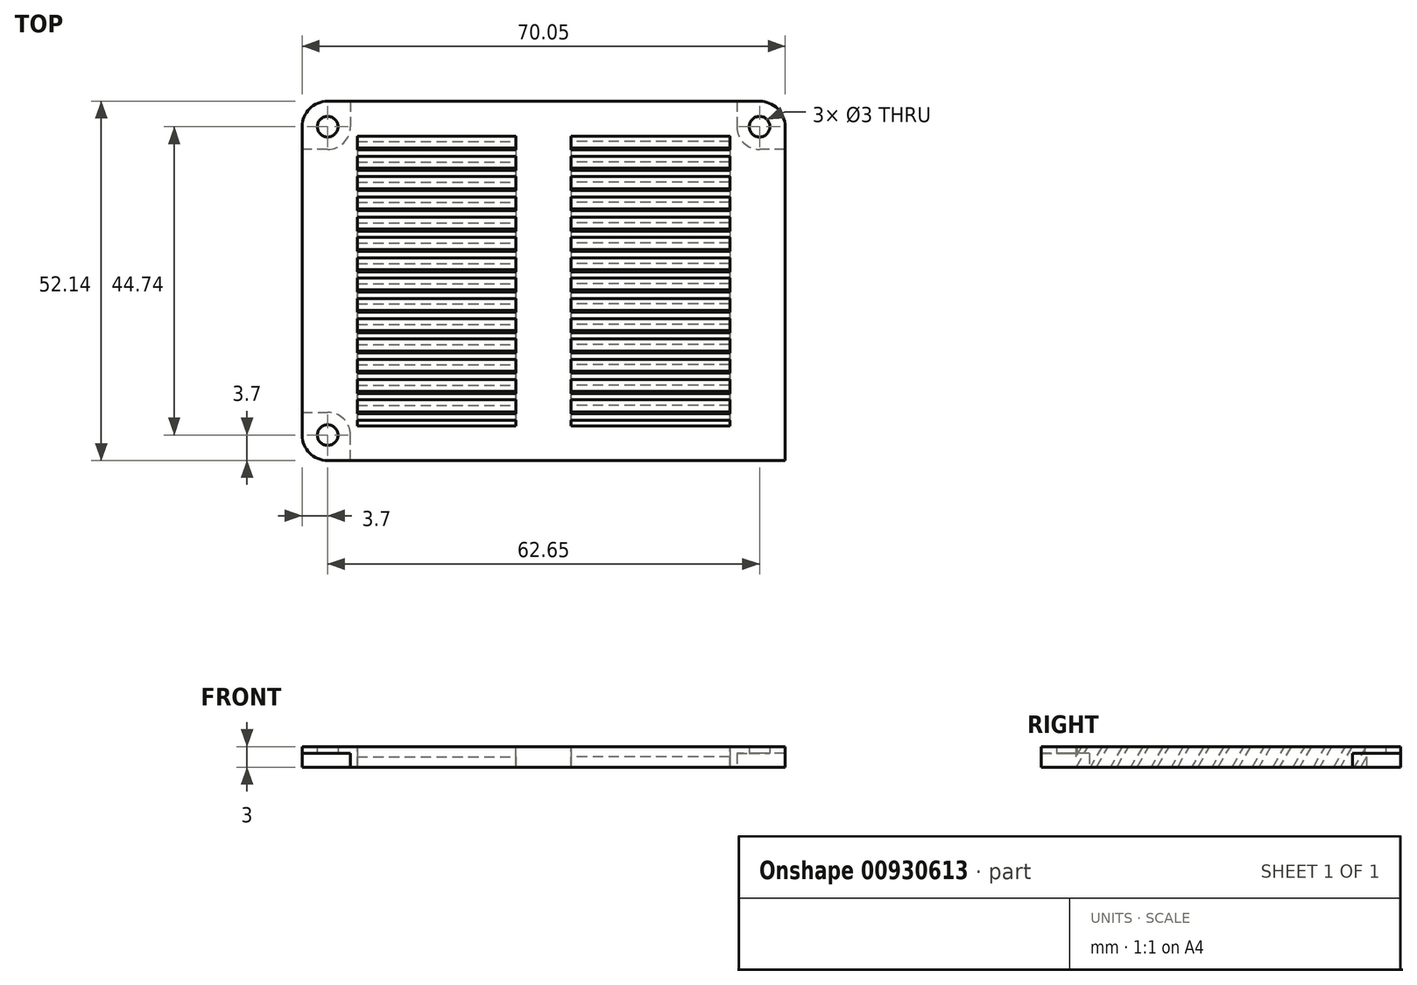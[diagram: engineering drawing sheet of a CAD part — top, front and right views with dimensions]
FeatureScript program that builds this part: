
annotation { "Feature Type Name" : "Feature", "Feature Type Description" : "" }
export const myFeature = defineFeature(function(context is Context, id is Id, definition is map)
    precondition{}
    {
        {
            var Q0;
            Q0=qCreatedBy(makeId("Top.planeOp"),FACE);
            var sketch = newSketch(context, id + "F0", { "sketchPlane" : qUnion([Q0])});
            skLineSegment(sketch, "E0", {"start": v(0, 0) * mm, "end": v(0, 44.74) * mm, "construction": true});
            skArc(sketch, "E1", {"start": v(4, 48.74) * mm, "mid": v(1.17, 47.57) * mm, "end": v(0, 44.74) * mm, "construction": true});
            skLineSegment(sketch, "E2", {"start": v(4, 48.74) * mm, "end": v(66.65, 48.74) * mm, "construction": true});
            skArc(sketch, "E3", {"start": v(70.65, 44.74) * mm, "mid": v(69.48, 47.57) * mm, "end": v(66.65, 48.74) * mm, "construction": true});
            skLineSegment(sketch, "E4", {"start": v(70.65, 44.74) * mm, "end": v(70.65, -4) * mm, "construction": true});
            skLineSegment(sketch, "E5", {"start": v(70.65, -4) * mm, "end": v(4, -4) * mm, "construction": true});
            skArc(sketch, "E6", {"start": v(0, 0) * mm, "mid": v(1.17, -2.83) * mm, "end": v(4, -4) * mm, "construction": true});
            skCircle(sketch, "E7", {"center": v(4, 44.74) * mm, "radius": 1.2 * mm, "construction": true});
            skCircle(sketch, "E8", {"center": v(4, 0) * mm, "radius": 1.2 * mm, "construction": true});
            skCircle(sketch, "E9", {"center": v(66.65, 44.74) * mm, "radius": 1.2 * mm, "construction": true});
            skLineSegment(sketch, "E10", {"start": v(0, 41.74) * mm, "end": v(4, 41.74) * mm, "construction": true});
            skLineSegment(sketch, "E11", {"start": v(7, 48.74) * mm, "end": v(7, 44.74) * mm, "construction": true});
            skArc(sketch, "E12", {"start": v(4, 41.74) * mm, "mid": v(6.12, 42.62) * mm, "end": v(7, 44.74) * mm, "construction": true});
            skLineSegment(sketch, "E13", {"start": v(63.65, 48.74) * mm, "end": v(63.65, 44.74) * mm, "construction": true});
            skLineSegment(sketch, "E14", {"start": v(70.65, 41.74) * mm, "end": v(66.65, 41.74) * mm, "construction": true});
            skArc(sketch, "E15", {"start": v(63.65, 44.74) * mm, "mid": v(64.53, 42.62) * mm, "end": v(66.65, 41.74) * mm, "construction": true});
            skLineSegment(sketch, "E16", {"start": v(0, 3) * mm, "end": v(4, 3) * mm, "construction": true});
            skLineSegment(sketch, "E17", {"start": v(7, -4) * mm, "end": v(7, 0) * mm, "construction": true});
            skArc(sketch, "E18", {"start": v(7, 0) * mm, "mid": v(6.12, 2.12) * mm, "end": v(4, 3) * mm, "construction": true});
            skSolve(sketch);
        }
        {
            var Q0;
            Q0=qCreatedBy(makeId("Top.planeOp"),FACE);
            var sketch = newSketch(context, id + "F1", { "sketchPlane" : qUnion([Q0])});
            skLineSegment(sketch, "E19", {"start": v(0.3, 44.74) * mm, "end": v(0.3, 0) * mm});
            skLineSegment(sketch, "E20", {"start": v(4, 48.44) * mm, "end": v(66.65, 48.44) * mm});
            skLineSegment(sketch, "E21", {"start": v(4, -3.7) * mm, "end": v(70.35, -3.7) * mm});
            skLineSegment(sketch, "E22", {"start": v(70.35, -3.7) * mm, "end": v(70.35, 44.74) * mm});
            skArc(sketch, "E23", {"start": v(4, 48.44) * mm, "mid": v(1.38, 47.36) * mm, "end": v(0.3, 44.74) * mm});
            skArc(sketch, "E24", {"start": v(70.35, 44.74) * mm, "mid": v(69.27, 47.36) * mm, "end": v(66.65, 48.44) * mm});
            skArc(sketch, "E25", {"start": v(0.3, 0) * mm, "mid": v(1.38, -2.62) * mm, "end": v(4, -3.7) * mm});
            skCircle(sketch, "E26", {"center": v(4, 44.74) * mm, "radius": 1.5 * mm});
            skCircle(sketch, "E27", {"center": v(66.65, 44.74) * mm, "radius": 1.5 * mm});
            skCircle(sketch, "E28", {"center": v(4, 0) * mm, "radius": 1.5 * mm});
            skLineSegment(sketch, "E29", {"start": v(35.32, 48.44) * mm, "end": v(35.32, -3.7) * mm, "construction": true});
            skLineSegment(sketch, "E30.bottom", {"start": v(8.3, 43.44) * mm, "end": v(31.33, 43.44) * mm});
            skLineSegment(sketch, "E30.top", {"start": v(8.3, 1.3) * mm, "end": v(31.33, 1.3) * mm});
            skLineSegment(sketch, "E30.left", {"start": v(8.3, 43.44) * mm, "end": v(8.3, 1.3) * mm});
            skLineSegment(sketch, "E30.right", {"start": v(31.33, 43.44) * mm, "end": v(31.33, 1.3) * mm});
            skLineSegment(sketch, "E31.bottom", {"start": v(39.32, 43.44) * mm, "end": v(62.35, 43.44) * mm});
            skLineSegment(sketch, "E31.top", {"start": v(39.32, 1.3) * mm, "end": v(62.35, 1.3) * mm});
            skLineSegment(sketch, "E31.left", {"start": v(39.32, 43.44) * mm, "end": v(39.32, 1.3) * mm});
            skLineSegment(sketch, "E31.right", {"start": v(62.35, 43.44) * mm, "end": v(62.35, 1.3) * mm});
            skSolve(sketch);
        }
        {
            var Q0;
            Q0=qSketchRegion(id+"F1",true);
            extrude(context, id + "F2", {"entities" : qUnion([Q0]), "depth" : 3 * mm, "offsetDistance" : 25 * mm});
        }
        {
            var Q0;
            Q0=makeQuery(id+"F2.opExtrude","SWEPT_FACE",FACE,{"disambiguationData":[OSD([sQuery(id+"F1.wireOp",EDGE,"E30.right")])]});
            var sketch = newSketch(context, id + "F3", { "sketchPlane" : qUnion([Q0])});
            skLineSegment(sketch, "E32", {"start": v(-22.37, 3) * mm, "end": v(-22.37, 0) * mm, "construction": true});
            skLineSegment(sketch, "E33", {"start": v(-21.5, 0) * mm, "end": v(-22.37, 1.5) * mm, "construction": true});
            skLineSegment(sketch, "E34", {"start": v(-22.37, 1.5) * mm, "end": v(-23.24, 3) * mm, "construction": true});
            skLineSegment(sketch, "E35", {"start": v(-23.7, 3) * mm, "end": v(-22.77, 3) * mm});
            skLineSegment(sketch, "E36", {"start": v(-22.77, 3) * mm, "end": v(-21.04, 0) * mm});
            skLineSegment(sketch, "E37", {"start": v(-21.04, 0) * mm, "end": v(-21.97, 0) * mm});
            skLineSegment(sketch, "E38", {"start": v(-21.97, 0) * mm, "end": v(-23.7, 3) * mm});
            skLineSegment(sketch, "E39", {"start": v(-20.75, 3) * mm, "end": v(-19.83, 3) * mm});
            skLineSegment(sketch, "E40", {"start": v(-19.83, 3) * mm, "end": v(-18.1, 0) * mm});
            skLineSegment(sketch, "E41", {"start": v(-18.1, 0) * mm, "end": v(-19.02, 0) * mm});
            skLineSegment(sketch, "E42", {"start": v(-19.02, 0) * mm, "end": v(-20.75, 3) * mm});
            skLineSegment(sketch, "E43", {"start": v(-17.8, 3) * mm, "end": v(-16.89, 3) * mm});
            skLineSegment(sketch, "E44", {"start": v(-16.89, 3) * mm, "end": v(-15.15, 0) * mm});
            skLineSegment(sketch, "E45", {"start": v(-15.15, 0) * mm, "end": v(-16.08, 0) * mm});
            skLineSegment(sketch, "E46", {"start": v(-16.08, 0) * mm, "end": v(-17.8, 3) * mm});
            skLineSegment(sketch, "E47", {"start": v(-14.86, 3) * mm, "end": v(-13.94, 3) * mm});
            skLineSegment(sketch, "E48", {"start": v(-13.94, 3) * mm, "end": v(-12.2, 0) * mm});
            skLineSegment(sketch, "E49", {"start": v(-12.2, 0) * mm, "end": v(-13.13, 0) * mm});
            skLineSegment(sketch, "E50", {"start": v(-13.13, 0) * mm, "end": v(-14.86, 3) * mm});
            skLineSegment(sketch, "E51", {"start": v(-11.92, 3) * mm, "end": v(-11, 3) * mm});
            skLineSegment(sketch, "E52", {"start": v(-11, 3) * mm, "end": v(-9.26, 0) * mm});
            skLineSegment(sketch, "E53", {"start": v(-9.26, 0) * mm, "end": v(-10.19, 0) * mm});
            skLineSegment(sketch, "E54", {"start": v(-10.19, 0) * mm, "end": v(-11.92, 3) * mm});
            skLineSegment(sketch, "E55", {"start": v(-8.98, 3) * mm, "end": v(-8.05, 3) * mm});
            skLineSegment(sketch, "E56", {"start": v(-8.05, 3) * mm, "end": v(-6.32, 0) * mm});
            skLineSegment(sketch, "E57", {"start": v(-6.32, 0) * mm, "end": v(-7.24, 0) * mm});
            skLineSegment(sketch, "E58", {"start": v(-7.24, 0) * mm, "end": v(-8.98, 3) * mm});
            skLineSegment(sketch, "E59", {"start": v(-6.03, 3) * mm, "end": v(-5.1, 3) * mm});
            skLineSegment(sketch, "E60", {"start": v(-5.1, 3) * mm, "end": v(-3.38, 0) * mm});
            skLineSegment(sketch, "E61", {"start": v(-3.38, 0) * mm, "end": v(-4.3, 0) * mm});
            skLineSegment(sketch, "E62", {"start": v(-4.3, 0) * mm, "end": v(-6.03, 3) * mm});
            skLineSegment(sketch, "E63", {"start": v(-1.35, 0) * mm, "end": v(-3.09, 3) * mm});
            skLineSegment(sketch, "E64", {"start": v(-25.72, 3) * mm, "end": v(-26.64, 3) * mm});
            skLineSegment(sketch, "E65", {"start": v(-26.64, 3) * mm, "end": v(-24.91, 0) * mm});
            skLineSegment(sketch, "E66", {"start": v(-24.91, 0) * mm, "end": v(-23.99, 0) * mm});
            skLineSegment(sketch, "E67", {"start": v(-23.99, 0) * mm, "end": v(-25.72, 3) * mm});
            skLineSegment(sketch, "E68", {"start": v(-28.66, 3) * mm, "end": v(-26.93, 0) * mm});
            skLineSegment(sketch, "E69", {"start": v(-26.93, 0) * mm, "end": v(-27.85, 0) * mm});
            skLineSegment(sketch, "E70", {"start": v(-27.85, 0) * mm, "end": v(-29.59, 3) * mm});
            skLineSegment(sketch, "E71", {"start": v(-29.59, 3) * mm, "end": v(-28.66, 3) * mm});
            skLineSegment(sketch, "E72", {"start": v(-31.6, 3) * mm, "end": v(-32.53, 3) * mm});
            skLineSegment(sketch, "E73", {"start": v(-32.53, 3) * mm, "end": v(-30.8, 0) * mm});
            skLineSegment(sketch, "E74", {"start": v(-30.8, 0) * mm, "end": v(-29.88, 0) * mm});
            skLineSegment(sketch, "E75", {"start": v(-29.88, 0) * mm, "end": v(-31.6, 3) * mm});
            skLineSegment(sketch, "E76", {"start": v(-34.55, 3) * mm, "end": v(-35.48, 3) * mm});
            skLineSegment(sketch, "E77", {"start": v(-35.48, 3) * mm, "end": v(-33.74, 0) * mm});
            skLineSegment(sketch, "E78", {"start": v(-33.74, 0) * mm, "end": v(-32.82, 0) * mm});
            skLineSegment(sketch, "E79", {"start": v(-32.82, 0) * mm, "end": v(-34.55, 3) * mm});
            skLineSegment(sketch, "E80", {"start": v(-38.42, 3) * mm, "end": v(-37.5, 3) * mm});
            skLineSegment(sketch, "E81", {"start": v(-37.5, 3) * mm, "end": v(-35.76, 0) * mm});
            skLineSegment(sketch, "E82", {"start": v(-35.76, 0) * mm, "end": v(-36.69, 0) * mm});
            skLineSegment(sketch, "E83", {"start": v(-36.69, 0) * mm, "end": v(-38.42, 3) * mm});
            skLineSegment(sketch, "E84", {"start": v(-40.44, 3) * mm, "end": v(-41.36, 3) * mm});
            skLineSegment(sketch, "E85", {"start": v(-41.36, 3) * mm, "end": v(-39.63, 0) * mm});
            skLineSegment(sketch, "E86", {"start": v(-39.63, 0) * mm, "end": v(-38.7, 0) * mm});
            skLineSegment(sketch, "E87", {"start": v(-38.7, 0) * mm, "end": v(-40.44, 3) * mm});
            skLineSegment(sketch, "E88", {"start": v(-41.65, 0) * mm, "end": v(-43.39, 3) * mm});
            skLineSegment(sketch, "E89", {"start": v(-41.65, 0) * mm, "end": v(-42.58, 0) * mm});
            skLineSegment(sketch, "E90", {"start": v(-42.58, 0) * mm, "end": v(-43.44, 1.5) * mm});
            skLineSegment(sketch, "E91", {"start": v(-43.44, 1.5) * mm, "end": v(-43.44, 3) * mm});
            skLineSegment(sketch, "E92", {"start": v(-43.44, 3) * mm, "end": v(-43.39, 3) * mm});
            skLineSegment(sketch, "E93", {"start": v(-1.3, 0) * mm, "end": v(-1.35, 0) * mm});
            skLineSegment(sketch, "E94", {"start": v(-1.3, 0) * mm, "end": v(-1.3, 1.5) * mm});
            skLineSegment(sketch, "E95", {"start": v(-1.3, 1.5) * mm, "end": v(-2.16, 3) * mm});
            skLineSegment(sketch, "E96", {"start": v(-2.16, 3) * mm, "end": v(-3.09, 3) * mm});
            skSolve(sketch);
        }
        {
            var Q0;
            Q0=qSketchRegion(id+"F3",true);
            extrude(context, id + "F4", {"entities" : qUnion([Q0]), "operationType" : NewBodyOperationType.ADD, "depth" : 23.02 * mm, "offsetDistance" : 25 * mm});
        }
        {
            var Q0;
            Q0=makeQuery(id+"F2.opExtrude","SWEPT_FACE",FACE,{"disambiguationData":[OSD([sQuery(id+"F1.wireOp",EDGE,"E31.left")])]});
            var sketch = newSketch(context, id + "F5", { "sketchPlane" : qUnion([Q0])});
            skLineSegment(sketch, "E97", {"start": v(22.37, 3) * mm, "end": v(22.37, 0) * mm, "construction": true});
            skLineSegment(sketch, "E98", {"start": v(21.5, 0) * mm, "end": v(22.37, 1.5) * mm, "construction": true});
            skLineSegment(sketch, "E99", {"start": v(22.37, 1.5) * mm, "end": v(23.24, 3) * mm, "construction": true});
            skLineSegment(sketch, "E100", {"start": v(22.77, 3) * mm, "end": v(21.04, 0) * mm});
            skLineSegment(sketch, "E101", {"start": v(21.04, 0) * mm, "end": v(21.97, 0) * mm});
            skLineSegment(sketch, "E102", {"start": v(21.97, 0) * mm, "end": v(23.7, 3) * mm});
            skLineSegment(sketch, "E103", {"start": v(22.77, 3) * mm, "end": v(23.7, 3) * mm});
            skLineSegment(sketch, "E104", {"start": v(25.72, 3) * mm, "end": v(26.64, 3) * mm});
            skLineSegment(sketch, "E105", {"start": v(26.64, 3) * mm, "end": v(24.91, 0) * mm});
            skLineSegment(sketch, "E106", {"start": v(24.91, 0) * mm, "end": v(23.99, 0) * mm});
            skLineSegment(sketch, "E107", {"start": v(23.99, 0) * mm, "end": v(25.72, 3) * mm});
            skLineSegment(sketch, "E108", {"start": v(28.66, 3) * mm, "end": v(29.59, 3) * mm});
            skLineSegment(sketch, "E109", {"start": v(29.59, 3) * mm, "end": v(27.85, 0) * mm});
            skLineSegment(sketch, "E110", {"start": v(27.85, 0) * mm, "end": v(26.93, 0) * mm});
            skLineSegment(sketch, "E111", {"start": v(26.93, 0) * mm, "end": v(28.66, 3) * mm});
            skLineSegment(sketch, "E112", {"start": v(31.6, 3) * mm, "end": v(32.53, 3) * mm});
            skLineSegment(sketch, "E113", {"start": v(32.53, 3) * mm, "end": v(30.8, 0) * mm});
            skLineSegment(sketch, "E114", {"start": v(30.8, 0) * mm, "end": v(29.88, 0) * mm});
            skLineSegment(sketch, "E115", {"start": v(29.88, 0) * mm, "end": v(31.6, 3) * mm});
            skLineSegment(sketch, "E116", {"start": v(34.55, 3) * mm, "end": v(35.48, 3) * mm});
            skLineSegment(sketch, "E117", {"start": v(35.48, 3) * mm, "end": v(33.74, 0) * mm});
            skLineSegment(sketch, "E118", {"start": v(33.74, 0) * mm, "end": v(32.82, 0) * mm});
            skLineSegment(sketch, "E119", {"start": v(32.82, 0) * mm, "end": v(34.55, 3) * mm});
            skLineSegment(sketch, "E120", {"start": v(37.5, 3) * mm, "end": v(38.42, 3) * mm});
            skLineSegment(sketch, "E121", {"start": v(38.42, 3) * mm, "end": v(36.69, 0) * mm});
            skLineSegment(sketch, "E122", {"start": v(36.69, 0) * mm, "end": v(35.76, 0) * mm});
            skLineSegment(sketch, "E123", {"start": v(35.76, 0) * mm, "end": v(37.5, 3) * mm});
            skLineSegment(sketch, "E124", {"start": v(40.44, 3) * mm, "end": v(41.36, 3) * mm});
            skLineSegment(sketch, "E125", {"start": v(41.36, 3) * mm, "end": v(39.63, 0) * mm});
            skLineSegment(sketch, "E126", {"start": v(39.63, 0) * mm, "end": v(38.7, 0) * mm});
            skLineSegment(sketch, "E127", {"start": v(38.7, 0) * mm, "end": v(40.44, 3) * mm});
            skLineSegment(sketch, "E128", {"start": v(43.44, 3) * mm, "end": v(43.39, 3) * mm});
            skLineSegment(sketch, "E129", {"start": v(43.39, 3) * mm, "end": v(41.65, 0) * mm});
            skLineSegment(sketch, "E130", {"start": v(41.65, 0) * mm, "end": v(42.58, 0) * mm});
            skLineSegment(sketch, "E131", {"start": v(43.44, 3) * mm, "end": v(43.44, 1.5) * mm});
            skLineSegment(sketch, "E132", {"start": v(43.44, 1.5) * mm, "end": v(42.58, 0) * mm});
            skLineSegment(sketch, "E133", {"start": v(20.75, 3) * mm, "end": v(19.83, 3) * mm});
            skLineSegment(sketch, "E134", {"start": v(19.83, 3) * mm, "end": v(18.1, 0) * mm});
            skLineSegment(sketch, "E135", {"start": v(18.1, 0) * mm, "end": v(19.02, 0) * mm});
            skLineSegment(sketch, "E136", {"start": v(19.02, 0) * mm, "end": v(20.75, 3) * mm});
            skLineSegment(sketch, "E137", {"start": v(17.8, 3) * mm, "end": v(16.89, 3) * mm});
            skLineSegment(sketch, "E138", {"start": v(16.89, 3) * mm, "end": v(15.15, 0) * mm});
            skLineSegment(sketch, "E139", {"start": v(15.15, 0) * mm, "end": v(16.08, 0) * mm});
            skLineSegment(sketch, "E140", {"start": v(16.08, 0) * mm, "end": v(17.8, 3) * mm});
            skLineSegment(sketch, "E141", {"start": v(14.86, 3) * mm, "end": v(13.94, 3) * mm});
            skLineSegment(sketch, "E142", {"start": v(13.94, 3) * mm, "end": v(12.2, 0) * mm});
            skLineSegment(sketch, "E143", {"start": v(12.2, 0) * mm, "end": v(13.13, 0) * mm});
            skLineSegment(sketch, "E144", {"start": v(13.13, 0) * mm, "end": v(14.86, 3) * mm});
            skLineSegment(sketch, "E145", {"start": v(11.92, 3) * mm, "end": v(11, 3) * mm});
            skLineSegment(sketch, "E146", {"start": v(11, 3) * mm, "end": v(9.26, 0) * mm});
            skLineSegment(sketch, "E147", {"start": v(9.26, 0) * mm, "end": v(10.19, 0) * mm});
            skLineSegment(sketch, "E148", {"start": v(10.19, 0) * mm, "end": v(11.92, 3) * mm});
            skLineSegment(sketch, "E149", {"start": v(8.98, 3) * mm, "end": v(8.05, 3) * mm});
            skLineSegment(sketch, "E150", {"start": v(8.05, 3) * mm, "end": v(6.32, 0) * mm});
            skLineSegment(sketch, "E151", {"start": v(6.32, 0) * mm, "end": v(7.24, 0) * mm});
            skLineSegment(sketch, "E152", {"start": v(7.24, 0) * mm, "end": v(8.98, 3) * mm});
            skLineSegment(sketch, "E153", {"start": v(6.03, 3) * mm, "end": v(5.1, 3) * mm});
            skLineSegment(sketch, "E154", {"start": v(5.1, 3) * mm, "end": v(3.38, 0) * mm});
            skLineSegment(sketch, "E155", {"start": v(3.38, 0) * mm, "end": v(4.3, 0) * mm});
            skLineSegment(sketch, "E156", {"start": v(4.3, 0) * mm, "end": v(6.03, 3) * mm});
            skLineSegment(sketch, "E157", {"start": v(1.3, 0) * mm, "end": v(1.35, 0) * mm});
            skLineSegment(sketch, "E158", {"start": v(1.35, 0) * mm, "end": v(3.09, 3) * mm});
            skLineSegment(sketch, "E159", {"start": v(3.09, 3) * mm, "end": v(2.16, 3) * mm});
            skLineSegment(sketch, "E160", {"start": v(2.16, 3) * mm, "end": v(1.3, 1.5) * mm});
            skLineSegment(sketch, "E161", {"start": v(1.3, 1.5) * mm, "end": v(1.3, 0) * mm});
            skSolve(sketch);
        }
        {
            var Q0;
            Q0=qSketchRegion(id+"F5",true);
            extrude(context, id + "F6", {"entities" : qUnion([Q0]), "operationType" : NewBodyOperationType.ADD, "depth" : 23.02 * mm, "offsetDistance" : 25 * mm});
        }
        {
            var Q0;
            Q0=makeQuery(id+"F4.boolean.opBoolean","MERGE",FACE,{"derivedFrom":[makeQuery(id+"F2.opExtrude","CAP_FACE",FACE,{"disambiguationData":[OSD([sQuery(id+"F1.wireOp",EDGE,"E19"),sQuery(id+"F1.wireOp",EDGE,"E20"),sQuery(id+"F1.wireOp",EDGE,"E21"),sQuery(id+"F1.wireOp",EDGE,"E22"),sQuery(id+"F1.wireOp",EDGE,"E23"),sQuery(id+"F1.wireOp",EDGE,"E24"),sQuery(id+"F1.wireOp",EDGE,"E25"),sQuery(id+"F1.wireOp",EDGE,"E26"),sQuery(id+"F1.wireOp",EDGE,"E27"),sQuery(id+"F1.wireOp",EDGE,"E28"),sQuery(id+"F1.wireOp",EDGE,"E30.bottom"),sQuery(id+"F1.wireOp",EDGE,"E30.top"),sQuery(id+"F1.wireOp",EDGE,"E30.left"),sQuery(id+"F1.wireOp",EDGE,"E30.right"),sQuery(id+"F1.wireOp",EDGE,"E31.bottom"),sQuery(id+"F1.wireOp",EDGE,"E31.top"),sQuery(id+"F1.wireOp",EDGE,"E31.left"),sQuery(id+"F1.wireOp",EDGE,"E31.right")])],"isStart":true}),makeQuery(id+"F4.opExtrude","SWEPT_FACE",FACE,{"disambiguationData":[OSD([sQuery(id+"F3.wireOp",EDGE,"E37")])]}),makeQuery(id+"F4.opExtrude","SWEPT_FACE",FACE,{"disambiguationData":[OSD([sQuery(id+"F3.wireOp",EDGE,"E41")])]}),makeQuery(id+"F4.opExtrude","SWEPT_FACE",FACE,{"disambiguationData":[OSD([sQuery(id+"F3.wireOp",EDGE,"E45")])]}),makeQuery(id+"F4.opExtrude","SWEPT_FACE",FACE,{"disambiguationData":[OSD([sQuery(id+"F3.wireOp",EDGE,"E49")])]}),makeQuery(id+"F4.opExtrude","SWEPT_FACE",FACE,{"disambiguationData":[OSD([sQuery(id+"F3.wireOp",EDGE,"E53")])]}),makeQuery(id+"F4.opExtrude","SWEPT_FACE",FACE,{"disambiguationData":[OSD([sQuery(id+"F3.wireOp",EDGE,"E57")])]}),makeQuery(id+"F4.opExtrude","SWEPT_FACE",FACE,{"disambiguationData":[OSD([sQuery(id+"F3.wireOp",EDGE,"E61")])]}),makeQuery(id+"F4.opExtrude","SWEPT_FACE",FACE,{"disambiguationData":[OSD([sQuery(id+"F3.wireOp",EDGE,"MffNTJaK-zk3o-27eV-5Zdy-I0cKc3JH3Vid")])]}),makeQuery(id+"F4.opExtrude","SWEPT_FACE",FACE,{"disambiguationData":[OSD([sQuery(id+"F3.wireOp",EDGE,"E66")])]}),makeQuery(id+"F4.opExtrude","SWEPT_FACE",FACE,{"disambiguationData":[OSD([sQuery(id+"F3.wireOp",EDGE,"E69")])]}),makeQuery(id+"F4.opExtrude","SWEPT_FACE",FACE,{"disambiguationData":[OSD([sQuery(id+"F3.wireOp",EDGE,"E74")])]}),makeQuery(id+"F4.opExtrude","SWEPT_FACE",FACE,{"disambiguationData":[OSD([sQuery(id+"F3.wireOp",EDGE,"E78")])]}),makeQuery(id+"F4.opExtrude","SWEPT_FACE",FACE,{"disambiguationData":[OSD([sQuery(id+"F3.wireOp",EDGE,"E82")])]}),makeQuery(id+"F4.opExtrude","SWEPT_FACE",FACE,{"disambiguationData":[OSD([sQuery(id+"F3.wireOp",EDGE,"E86")])]}),makeQuery(id+"F4.opExtrude","SWEPT_FACE",FACE,{"disambiguationData":[OSD([sQuery(id+"F3.wireOp",EDGE,"7d4vqGJ6-KAj1-R2qT-3zMX-hT7wDYY7Z8Nv")])]})]});
            var sketch = newSketch(context, id + "F7", { "sketchPlane" : qUnion([Q0])});
            skLineSegment(sketch, "E162", {"start": v(7.3, 3.7) * mm, "end": v(7.3, 0) * mm});
            skLineSegment(sketch, "E163", {"start": v(0.3, -3.3) * mm, "end": v(4, -3.3) * mm});
            skArc(sketch, "E164", {"start": v(4, -3.3) * mm, "mid": v(6.33, -2.33) * mm, "end": v(7.3, 0) * mm});
            skLineSegment(sketch, "E165", {"start": v(0.3, -3.3) * mm, "end": v(0.3, 0) * mm});
            skLineSegment(sketch, "E166", {"start": v(7.3, 3.7) * mm, "end": v(4, 3.7) * mm});
            skArc(sketch, "E167", {"start": v(4, 3.7) * mm, "mid": v(1.38, 2.62) * mm, "end": v(0.3, 0) * mm});
            skArc(sketch, "E168", {"start": v(0.3, -44.74) * mm, "mid": v(1.38, -47.36) * mm, "end": v(4, -48.44) * mm});
            skArc(sketch, "E169", {"start": v(7.3, -44.74) * mm, "mid": v(6.33, -42.4) * mm, "end": v(4, -41.44) * mm});
            skLineSegment(sketch, "E170", {"start": v(4, -41.44) * mm, "end": v(0.3, -41.44) * mm});
            skLineSegment(sketch, "E171", {"start": v(0.3, -41.44) * mm, "end": v(0.3, -44.74) * mm});
            skLineSegment(sketch, "E172", {"start": v(4, -48.44) * mm, "end": v(7.3, -48.44) * mm});
            skLineSegment(sketch, "E173", {"start": v(7.3, -48.44) * mm, "end": v(7.3, -44.74) * mm});
            skArc(sketch, "E174", {"start": v(66.65, -48.44) * mm, "mid": v(69.27, -47.36) * mm, "end": v(70.35, -44.74) * mm});
            skLineSegment(sketch, "E175", {"start": v(66.65, -48.44) * mm, "end": v(63.35, -48.44) * mm});
            skLineSegment(sketch, "E176", {"start": v(63.35, -48.44) * mm, "end": v(63.35, -44.74) * mm});
            skLineSegment(sketch, "E177", {"start": v(70.35, -44.74) * mm, "end": v(70.35, -41.44) * mm});
            skLineSegment(sketch, "E178", {"start": v(70.35, -41.44) * mm, "end": v(66.65, -41.44) * mm});
            skArc(sketch, "E179", {"start": v(66.65, -41.44) * mm, "mid": v(64.32, -42.4) * mm, "end": v(63.35, -44.74) * mm});
            skSolve(sketch);
        }
        {
            var Q0;
            Q0=qSketchRegion(id+"F7",true);
            extrude(context, id + "F8", {"entities" : qUnion([Q0]), "operationType" : NewBodyOperationType.REMOVE, "oppositeDirection" : true, "depth" : 2 * mm, "offsetDistance" : 25 * mm});
        }
    });
